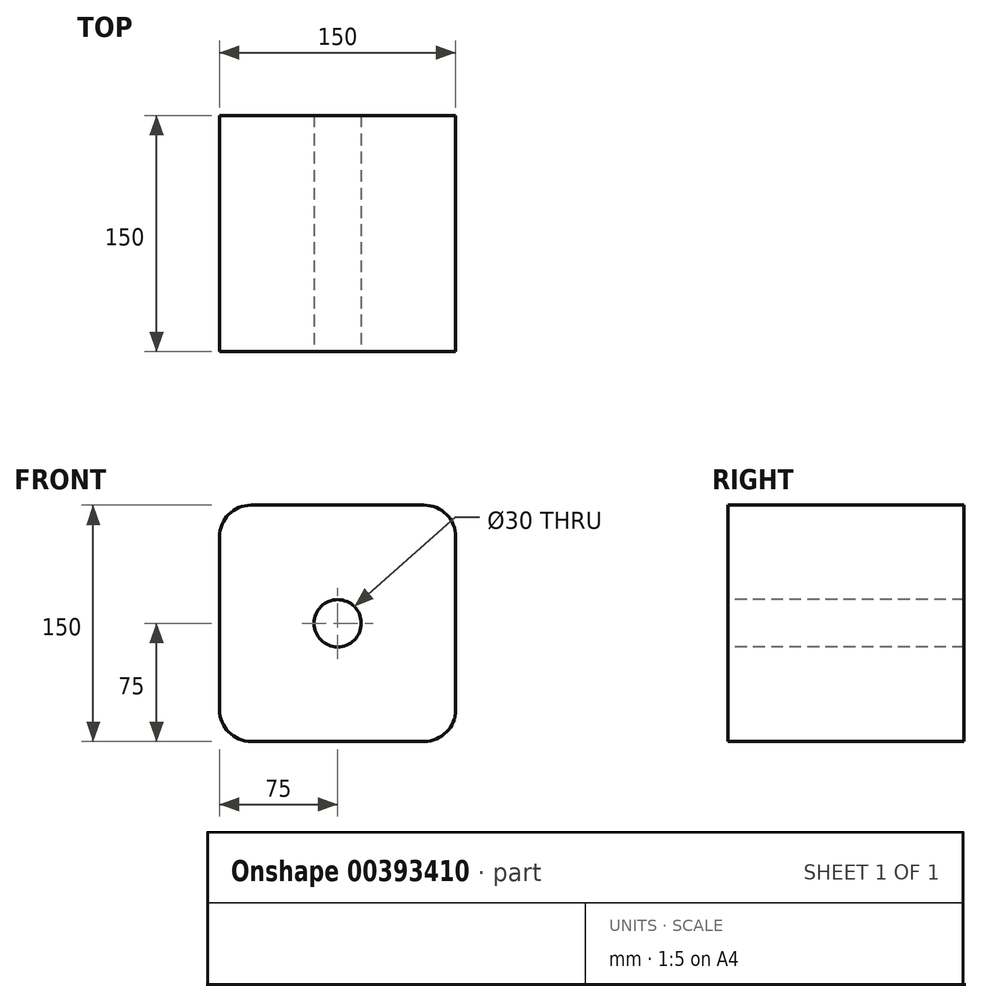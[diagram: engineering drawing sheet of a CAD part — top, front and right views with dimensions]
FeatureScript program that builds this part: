
annotation { "Feature Type Name" : "Feature", "Feature Type Description" : "" }
export const myFeature = defineFeature(function(context is Context, id is Id, definition is map)
    precondition{}
    {
        {
            var Q0;
            Q0=qCreatedBy(makeId("Front.planeOp"),FACE);
            var sketch = newSketch(context, id + "F0", { "sketchPlane" : qUnion([Q0])});
            skLineSegment(sketch, "E0.bottom", {"start": v(-55, 75) * mm, "end": v(55, 75) * mm});
            skLineSegment(sketch, "E0.top", {"start": v(-55, -75) * mm, "end": v(55, -75) * mm});
            skLineSegment(sketch, "E0.left", {"start": v(-75, 55) * mm, "end": v(-75, -55) * mm});
            skLineSegment(sketch, "E0.right", {"start": v(75, 55) * mm, "end": v(75, -55) * mm});
            skPoint(sketch, "E0.middle", {"position": v(0, 0) * mm});
            skPoint(sketch, "E1.visualSharp", {"position": v(-75, 75) * mm});
            skArc(sketch, "E1.filletArc", {"start": v(-55, 75) * mm, "mid": v(-69.14, 69.14) * mm, "end": v(-75, 55) * mm});
            skPoint(sketch, "E2.visualSharp", {"position": v(75, 75) * mm});
            skArc(sketch, "E2.filletArc", {"start": v(75, 55) * mm, "mid": v(69.14, 69.14) * mm, "end": v(55, 75) * mm});
            skPoint(sketch, "E3.visualSharp", {"position": v(75, -75) * mm});
            skArc(sketch, "E3.filletArc", {"start": v(55, -75) * mm, "mid": v(69.14, -69.14) * mm, "end": v(75, -55) * mm});
            skPoint(sketch, "E4.visualSharp", {"position": v(-75, -75) * mm});
            skArc(sketch, "E4.filletArc", {"start": v(-75, -55) * mm, "mid": v(-69.14, -69.14) * mm, "end": v(-55, -75) * mm});
            skSolve(sketch);
        }
        {
            var Q0;
            Q0=makeQuery(id+"F0.imprint","IMPRINT",FACE,{"disambiguationData":[TD([[makeQuery(id+"F0.imprint","IMPRINT",EDGE,{"derivedFrom":sQuery(id+"F0.wireOp",EDGE,"E0.bottom")}),-1.0]])]});
            extrude(context, id + "F1", {"entities" : qUnion([Q0]), "depth" : 150 * mm});
        }
        {
            var Q0;
            Q0=makeQuery(id+"F1.opExtrude","CAP_FACE",FACE,{"disambiguationData":[OSD([sQuery(id+"F0.wireOp",EDGE,"E0.bottom"),sQuery(id+"F0.wireOp",EDGE,"E0.top"),sQuery(id+"F0.wireOp",EDGE,"E0.left"),sQuery(id+"F0.wireOp",EDGE,"E0.right"),sQuery(id+"F0.wireOp",EDGE,"E1.filletArc"),sQuery(id+"F0.wireOp",EDGE,"E2.filletArc"),sQuery(id+"F0.wireOp",EDGE,"E3.filletArc"),sQuery(id+"F0.wireOp",EDGE,"E4.filletArc")])],"isStart":false});
            var sketch = newSketch(context, id + "F2", { "sketchPlane" : qUnion([Q0])});
            skCircle(sketch, "E5", {"center": v(0, 0) * mm, "radius": 15 * mm});
            skSolve(sketch);
        }
        {
            var Q0;
            Q0 = qSketchRegion(id + "F2", true);
            extrude(context, id + "F3", {"entities" : qUnion([Q0]), "operationType" : NewBodyOperationType.REMOVE, "endBound" : BoundingType.THROUGH_ALL, "oppositeDirection" : true, "depth" : 25 * mm});
        }
    });
